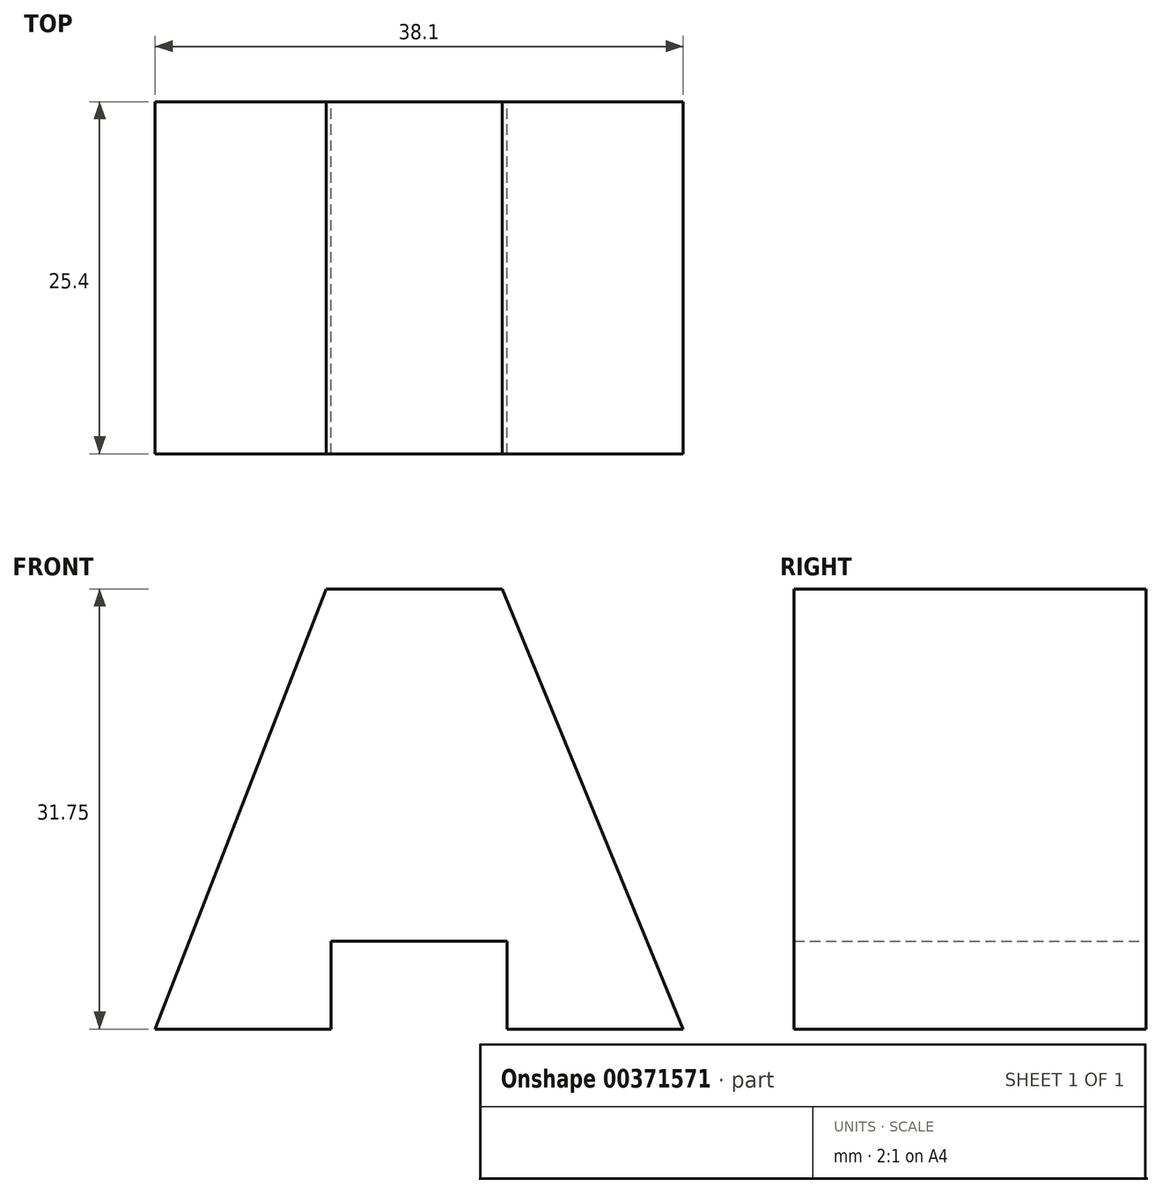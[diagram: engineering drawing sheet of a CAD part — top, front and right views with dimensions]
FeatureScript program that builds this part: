
annotation { "Feature Type Name" : "Feature", "Feature Type Description" : "" }
export const myFeature = defineFeature(function(context is Context, id is Id, definition is map)
    precondition{}
    {
        {
            var Q0;
            Q0=qCreatedBy(makeId("Front.planeOp"),FACE);
            var sketch = newSketch(context, id + "F0", { "sketchPlane" : qUnion([Q0])});
            skLineSegment(sketch, "E0", {"start": v(0, 0) * mm, "end": v(0, 31.75) * mm});
            skLineSegment(sketch, "E1", {"start": v(0, 31.75) * mm, "end": v(38.1, 31.75) * mm});
            skLineSegment(sketch, "E2", {"start": v(38.1, 31.75) * mm, "end": v(38.1, 0) * mm});
            skLineSegment(sketch, "E3", {"start": v(38.1, 0) * mm, "end": v(25.4, 0) * mm});
            skLineSegment(sketch, "E4", {"start": v(25.4, 0) * mm, "end": v(25.4, 6.35) * mm});
            skLineSegment(sketch, "E5", {"start": v(25.4, 6.35) * mm, "end": v(12.7, 6.35) * mm});
            skLineSegment(sketch, "E6", {"start": v(12.7, 6.35) * mm, "end": v(12.7, 0) * mm});
            skLineSegment(sketch, "E7", {"start": v(12.7, 0) * mm, "end": v(0, 0) * mm});
            skSolve(sketch);
        }
        {
            var Q0;
            Q0 = qSketchRegion(id + "F0", true);
            extrude(context, id + "F1", {"entities" : qUnion([Q0]), "depth" : 25.4 * mm});
        }
        {
            var Q0;
            Q0=makeQuery(id+"F1.opExtrude","CAP_FACE",FACE,{"disambiguationData":[OSD([sQuery(id+"F0.wireOp",EDGE,"E0"),sQuery(id+"F0.wireOp",EDGE,"E1"),sQuery(id+"F0.wireOp",EDGE,"E2"),sQuery(id+"F0.wireOp",EDGE,"E3"),sQuery(id+"F0.wireOp",EDGE,"E4"),sQuery(id+"F0.wireOp",EDGE,"E5"),sQuery(id+"F0.wireOp",EDGE,"E6"),sQuery(id+"F0.wireOp",EDGE,"E7")])],"isStart":false});
            var sketch = newSketch(context, id + "F2", { "sketchPlane" : qUnion([Q0])});
            skLineSegment(sketch, "E8", {"start": v(38.1, 0) * mm, "end": v(25.04, 31.75) * mm});
            skLineSegment(sketch, "E9", {"start": v(0, 0) * mm, "end": v(12.34, 31.75) * mm});
            skSolve(sketch);
        }
        {
            var Q0;
            Q0 = qSketchRegion(id + "F2", true);
            var Q1;
            {var subQ0=sQuery(id+"F2.wireOp",EDGE,"E9");Q1=makeQuery(id+"F2.imprint","IMPRINT",FACE,{"disambiguationData":[TD([[makeQuery(id+"F2.imprint","IMPRINT",EDGE,{"derivedFrom":subQ0}),1.0]])]});}
            var Q2;
            {var subQ0=sQuery(id+"F2.wireOp",EDGE,"E8");Q2=makeQuery(id+"F2.imprint","IMPRINT",FACE,{"disambiguationData":[TD([[makeQuery(id+"F2.imprint","IMPRINT",EDGE,{"derivedFrom":subQ0}),-1.0]])]});}
            extrude(context, id + "F3", {"entities" : qUnion([Q0, Q1, Q2]), "operationType" : NewBodyOperationType.REMOVE, "oppositeDirection" : true, "depth" : 25.4 * mm});
        }
    });
